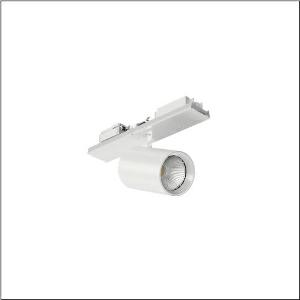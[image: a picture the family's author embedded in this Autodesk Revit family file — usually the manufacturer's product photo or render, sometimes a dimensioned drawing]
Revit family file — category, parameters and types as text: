
# Revit family: licross_r__spot_31_51sl127a45b_74df
name_source: partatom
category: Lighting Fixtures
units: mm (PartAtom-declared; Revit-internal decimal feet)

## family parameters
Cut with Voids When Loaded = No
Host = Face
Light Source = No
Part Type = Normal
Room Calculation Point = No
Round Connector Dimension = Use Diameter
Shared = No

## types (1)
- --- (1 x LED, 5140 lm, 42.6 W, 4000K)
    Apparent Load = 43 VA
    CIE Flux Codes = 93 97 99 100 100
    Color Rendering = 90
    Color Temperature = 4000K
    Default Elevation = 1800 mm
    Description = Licross® Spot 31, directional spotlight, light control with lens, of plastic, LED rated luminous flux: 5.140lm, light colour: 940, with plug, 3-pole, with phase selection, mains connection: 220..240V, AC, 50/60Hz, of aluminium, traffic white (RAL 9016), length: 140mm, diameter: 90mm, protection rating (complete): IP20, insulation class (complete): insulation class I (protective earthing), certification: CE, packaging unit: 1 piece
    Height = 175 mm
    Lamp = 1 x LED
    Lamp Light Flux = 5140 lm
    Lamp Power = 42.6 W
    Lamp count = 1
    Length = 90 mm
    Luminous efficacy = 121 lm/W
    Manufacturer = Siteco
    ModVariant = No
    Model = 51SL127A45B
    Mounting Place = Ceiling
    Mounting Type = Pendant
    Number of Poles = 1
    OnlyDefault = Yes
    Power Factor = 1
    Product Name = Licross® Spot 31
    Product group = directional spotlight
    ProductGroupID = 905
    Protection Class = Protection class I
    Protection Degree = IP 20
    RLX_Detail_Level = 1
    RLX_Emergency_Light_Flux = 0 lm
    RLX_Emergency_Type = 0
    RLX_Emergency_Type_DB = No
    RlxData = <blob elided: 14801 chars, md5=25ded316>
    Socket = socket
    Standby Power = 0 W
    System Light Flux = 5140 lm
    System Power = 43 W
    Type Comments = factory setting: luminous flux: 100 % | (ON | ON | ON) | 1050 mA
    Type Image = l_1245720.jpg
    URL = http://relux.com
    VarID = @adj_064071
    Voltage = 0 V
    Weight = 0.00 kg
    Width = 0 mm  [stored 0 ft]

note: [stored X ft] marks values corroborated as IEEE doubles in the binary element streams (Revit-internal decimal feet)

## geometry (parser evidence)
native form markers: Sweep x10
no freeform markers — native parametric forms only
